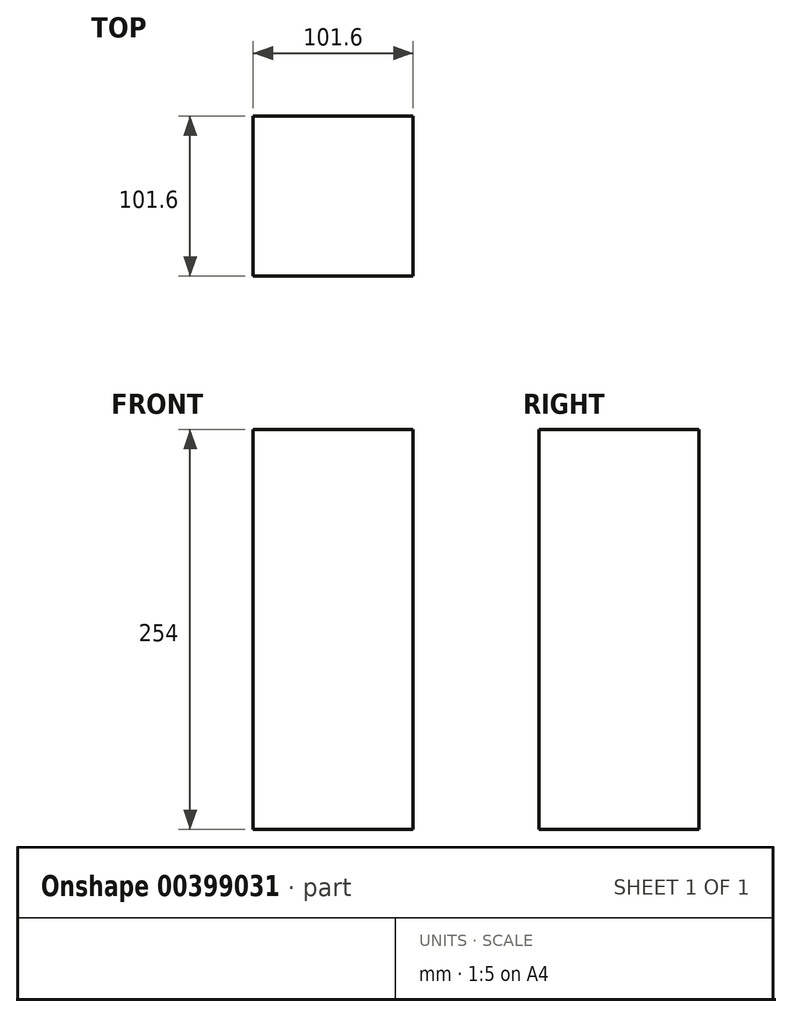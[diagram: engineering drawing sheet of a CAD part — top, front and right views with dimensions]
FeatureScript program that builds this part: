
annotation { "Feature Type Name" : "Feature", "Feature Type Description" : "" }
export const myFeature = defineFeature(function(context is Context, id is Id, definition is map)
    precondition{}
    {
        {
            var Q0;
            Q0=qCreatedBy(makeId("Top.planeOp"),FACE);
            var sketch = newSketch(context, id + "F0", { "sketchPlane" : qUnion([Q0])});
            skLineSegment(sketch, "E0.bottom", {"start": v(-50.8, 50.8) * mm, "end": v(50.8, 50.8) * mm});
            skLineSegment(sketch, "E0.top", {"start": v(-50.8, -50.8) * mm, "end": v(50.8, -50.8) * mm});
            skLineSegment(sketch, "E0.left", {"start": v(-50.8, 50.8) * mm, "end": v(-50.8, -50.8) * mm});
            skLineSegment(sketch, "E0.right", {"start": v(50.8, 50.8) * mm, "end": v(50.8, -50.8) * mm});
            skPoint(sketch, "E0.middle", {"position": v(0, 0) * mm});
            skSolve(sketch);
        }
        {
            var Q0;
            Q0 = qSketchRegion(id + "F0", true);
            extrude(context, id + "F1", {"entities" : qUnion([Q0]), "depth" : 254 * mm});
        }
    });
